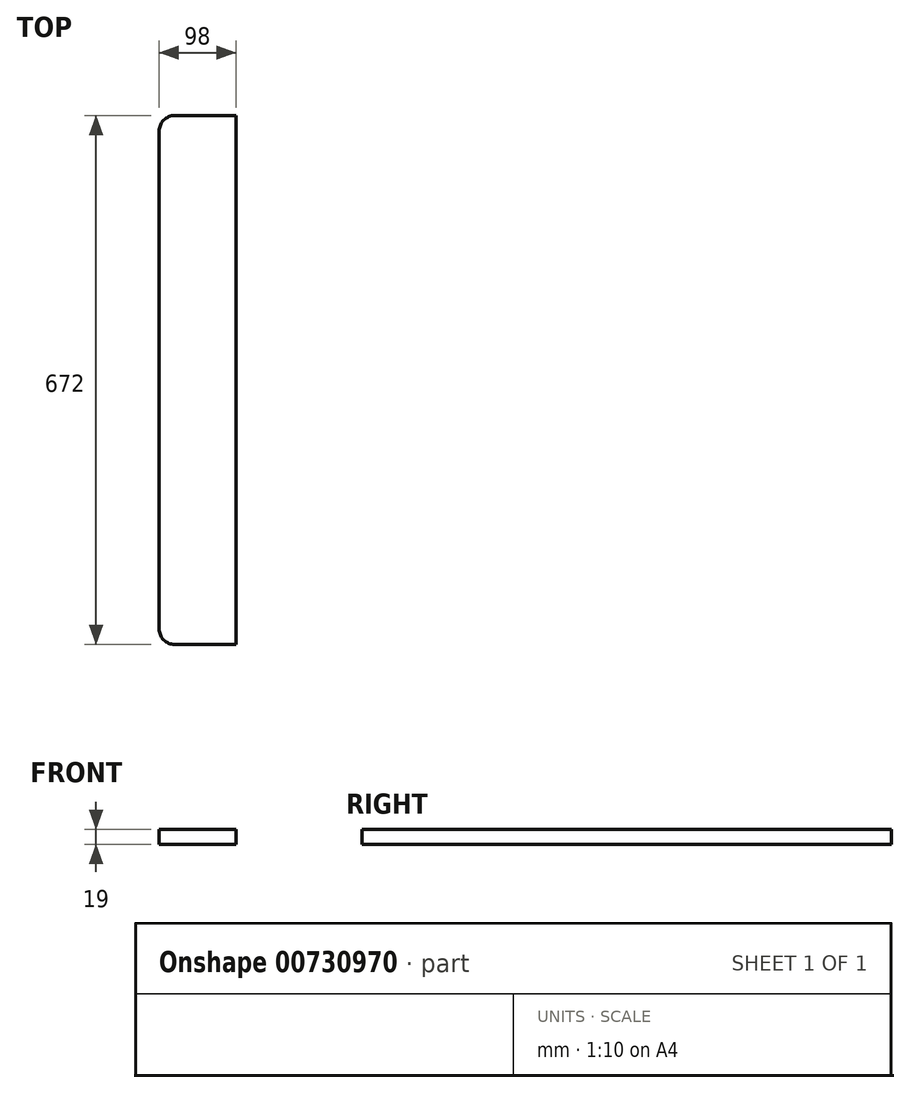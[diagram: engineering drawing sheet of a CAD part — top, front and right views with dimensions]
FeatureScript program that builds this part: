
annotation { "Feature Type Name" : "Feature", "Feature Type Description" : "" }
export const myFeature = defineFeature(function(context is Context, id is Id, definition is map)
    precondition{}
    {
        {
            var Q0;
            Q0=qCreatedBy(makeId("Front.planeOp"),FACE);
            var sketch = newSketch(context, id + "F0", { "sketchPlane" : qUnion([Q0])});
            skLineSegment(sketch, "E0.bottom", {"start": v(49, -9.5) * mm, "end": v(-49, -9.5) * mm});
            skLineSegment(sketch, "E0.top", {"start": v(49, 9.5) * mm, "end": v(-49, 9.5) * mm});
            skLineSegment(sketch, "E0.left", {"start": v(49, -9.5) * mm, "end": v(49, 9.5) * mm});
            skLineSegment(sketch, "E0.right", {"start": v(-49, -9.5) * mm, "end": v(-49, 9.5) * mm});
            skPoint(sketch, "E0.middle", {"position": v(0, 0) * mm});
            skSolve(sketch);
        }
        {
            var Q0;
            Q0=makeQuery(id+"F0.imprint","IMPRINT",FACE,{"disambiguationData":[TD([[makeQuery(id+"F0.imprint","IMPRINT",EDGE,{"derivedFrom":sQuery(id+"F0.wireOp",EDGE,"E0.bottom")}),-1.0]])]});
            extrude(context, id + "F1", {"entities" : qUnion([Q0]), "depth" : 672 * mm, "offsetDistance" : 25 * mm});
        }
        {
            var Q0;
            Q0=makeQuery(id+"F1.opExtrude","CAP_EDGE",EDGE,{"disambiguationData":[OSD([sQuery(id+"F0.wireOp",EDGE,"E0.right")])],"isStart":false});
            var Q1;
            Q1=makeQuery(id+"F1.opExtrude","CAP_EDGE",EDGE,{"disambiguationData":[OSD([sQuery(id+"F0.wireOp",EDGE,"E0.right")])],"isStart":true});
            fillet(context, id + "F2", {"entities" : qUnion([Q0, Q1]), "radius" : 20 * mm, "tangentPropagation" : true, "allowEdgeOverflow" : false});
        }
    });
